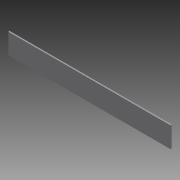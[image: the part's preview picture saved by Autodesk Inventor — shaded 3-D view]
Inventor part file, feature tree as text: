
AUTODESK INVENTOR PART (.ipt)
format: ipt  version: 2011 (Build 150239000, 239)  size: 65,024 bytes
history: native  units: in
note: dims shown in document units (in); Inventor stores cm internally (conversion verified against a paired STEP export)
features: extrude x1, sketch x1
ambient origin geometry x8: Origin, YZ Plane, XZ Plane, XY Plane, X Axis, Y Axis, Z Axis, Center Point
bodies: Solid1 (feature_tree)
feature tree (2):
  extrude  "Extrusion1"  Depth=2.0in
  sketch  "Sketch1"  dims[d0=15.748in d1=2.0in d2=0.125in d3=0.0in]
